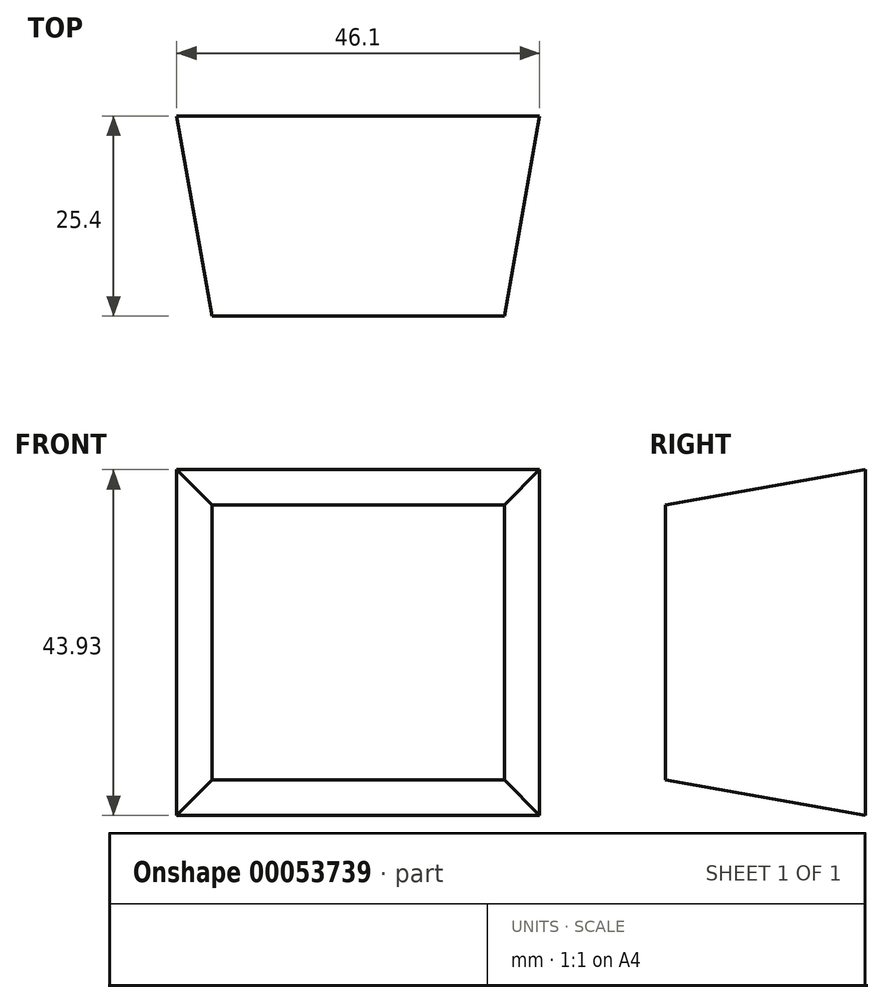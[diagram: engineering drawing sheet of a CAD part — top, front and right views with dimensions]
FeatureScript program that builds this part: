
annotation { "Feature Type Name" : "Feature", "Feature Type Description" : "" }
export const myFeature = defineFeature(function(context is Context, id is Id, definition is map)
    precondition{}
    {
        {
            var Q0;
            Q0=qCreatedBy(makeId("Front.planeOp"),FACE);
            var sketch = newSketch(context, id + "F0", { "sketchPlane" : qUnion([Q0])});
            skLineSegment(sketch, "E0.bottom", {"start": v(0, 0) * mm, "end": v(46.1, 0) * mm});
            skLineSegment(sketch, "E0.top", {"start": v(0, 43.93) * mm, "end": v(46.1, 43.93) * mm});
            skLineSegment(sketch, "E0.left", {"start": v(0, 0) * mm, "end": v(0, 43.93) * mm});
            skLineSegment(sketch, "E0.right", {"start": v(46.1, 0) * mm, "end": v(46.1, 43.93) * mm});
            skSolve(sketch);
        }
        {
            var Q0;
            Q0=makeQuery(id+"F0.imprint","IMPRINT",FACE,{"disambiguationData":[TD([[makeQuery(id+"F0.imprint","IMPRINT",EDGE,{"derivedFrom":sQuery(id+"F0.wireOp",EDGE,"E0.bottom")}),1.0]])]});
            extrude(context, id + "F1", {"entities" : qUnion([Q0]), "depth" : 25.4 * mm, "hasDraft" : true, "draftAngle" : 10 * degree, "draftPullDirection" : true});
        }
    });
